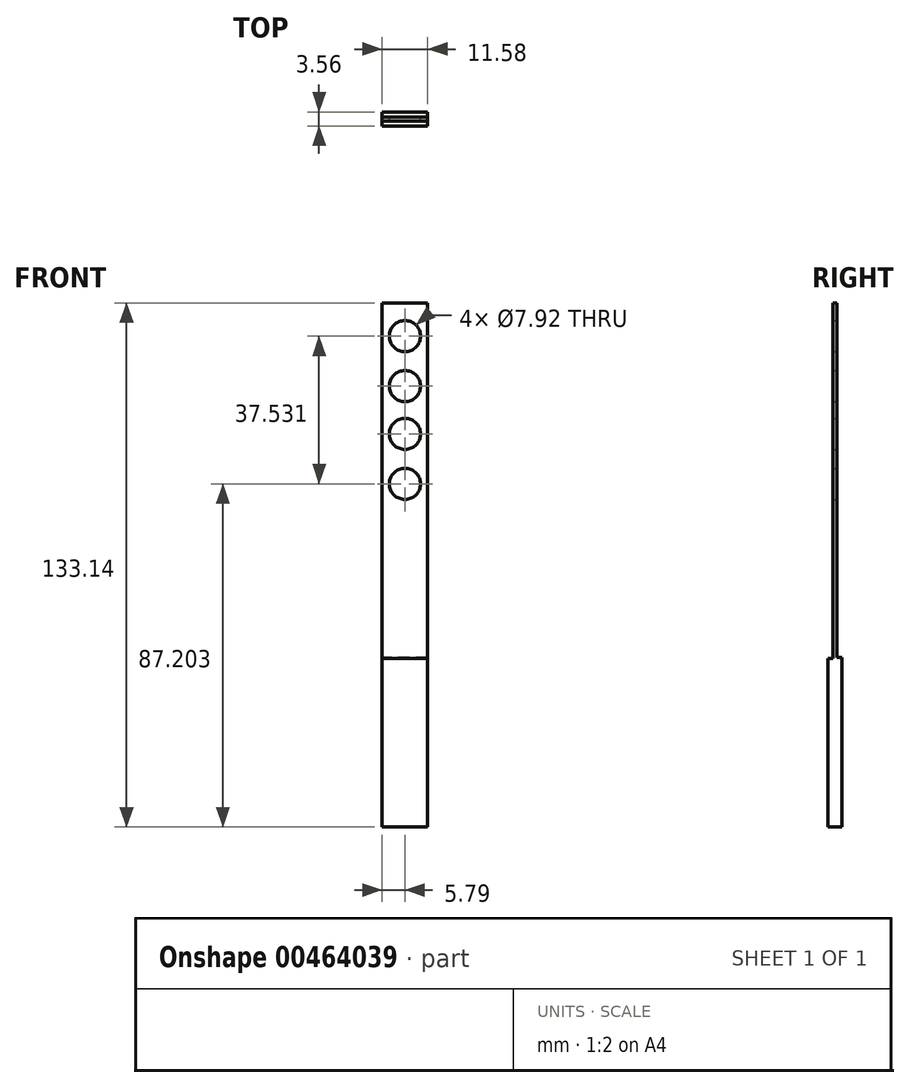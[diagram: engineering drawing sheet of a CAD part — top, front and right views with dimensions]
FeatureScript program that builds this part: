
annotation { "Feature Type Name" : "Feature", "Feature Type Description" : "" }
export const myFeature = defineFeature(function(context is Context, id is Id, definition is map)
    precondition{}
    {
        {
            var Q0;
            Q0=qCreatedBy(makeId("Front.planeOp"),FACE);
            var sketch = newSketch(context, id + "F0", { "sketchPlane" : qUnion([Q0])});
            skLineSegment(sketch, "E0.bottom", {"start": v(-5.79, 66.57) * mm, "end": v(5.79, 66.57) * mm});
            skLineSegment(sketch, "E0.top", {"start": v(-5.79, -66.57) * mm, "end": v(5.79, -66.57) * mm});
            skLineSegment(sketch, "E0.left", {"start": v(-5.79, 66.57) * mm, "end": v(-5.79, -66.57) * mm});
            skLineSegment(sketch, "E0.right", {"start": v(5.79, 66.57) * mm, "end": v(5.79, -66.57) * mm});
            skPoint(sketch, "E0.middle", {"position": v(0, 0) * mm});
            skCircle(sketch, "E1", {"center": v(0, 58.16) * mm, "radius": 3.96 * mm});
            skCircle(sketch, "E2", {"center": v(0, 45.47) * mm, "radius": 3.96 * mm});
            skCircle(sketch, "E3", {"center": v(0, 33.33) * mm, "radius": 3.96 * mm});
            skCircle(sketch, "E4", {"center": v(0, 20.63) * mm, "radius": 3.96 * mm});
            skSolve(sketch);
        }
        {
            var Q0;
            Q0=makeQuery(id+"F0.imprint","IMPRINT",FACE,{"disambiguationData":[TD([[makeQuery(id+"F0.imprint","IMPRINT",EDGE,{"derivedFrom":sQuery(id+"F0.wireOp",EDGE,"E0.bottom")}),-1.0]])]});
            extrude(context, id + "F1", {"entities" : qUnion([Q0]), "depth" : 1.02 * mm});
        }
        {
            var Q0;
            Q0=makeQuery(id+"F1.opExtrude","CAP_FACE",FACE,{"disambiguationData":[OSD([sQuery(id+"F0.wireOp",EDGE,"E0.bottom"),sQuery(id+"F0.wireOp",EDGE,"E0.top"),sQuery(id+"F0.wireOp",EDGE,"E0.left"),sQuery(id+"F0.wireOp",EDGE,"E0.right"),sQuery(id+"F0.wireOp",EDGE,"E1"),sQuery(id+"F0.wireOp",EDGE,"E2"),sQuery(id+"F0.wireOp",EDGE,"E3"),sQuery(id+"F0.wireOp",EDGE,"E4")])],"isStart":false});
            var sketch = newSketch(context, id + "F2", { "sketchPlane" : qUnion([Q0])});
            skLineSegment(sketch, "E5", {"start": v(-5.79, -23.68) * mm, "end": v(5.79, -23.68) * mm});
            skSolve(sketch);
        }
        {
            var Q0;
            Q0 = qSketchRegion(id + "F2", true);
            var Q1;
            {var subQ0=sQuery(id+"F2.wireOp",EDGE,"E5");Q1=makeQuery(id+"F2.imprint","IMPRINT",FACE,{"disambiguationData":[TD([[makeQuery(id+"F2.imprint","IMPRINT",EDGE,{"derivedFrom":subQ0}),-1.0]])]});}
            extrude(context, id + "F3", {"entities" : qUnion([Q0, Q1]), "operationType" : NewBodyOperationType.ADD, "depth" : 1.27 * mm});
        }
        {
            var Q0;
            Q0=makeQuery(id+"F1.opExtrude","CAP_FACE",FACE,{"disambiguationData":[OSD([sQuery(id+"F0.wireOp",EDGE,"E0.bottom"),sQuery(id+"F0.wireOp",EDGE,"E0.top"),sQuery(id+"F0.wireOp",EDGE,"E0.left"),sQuery(id+"F0.wireOp",EDGE,"E0.right"),sQuery(id+"F0.wireOp",EDGE,"E1"),sQuery(id+"F0.wireOp",EDGE,"E2"),sQuery(id+"F0.wireOp",EDGE,"E3"),sQuery(id+"F0.wireOp",EDGE,"E4")])],"isStart":true});
            var sketch = newSketch(context, id + "F4", { "sketchPlane" : qUnion([Q0])});
            skLineSegment(sketch, "E6", {"start": v(-5.79, -23.52) * mm, "end": v(5.79, -23.52) * mm});
            skSolve(sketch);
        }
        {
            var Q0;
            Q0 = qSketchRegion(id + "F4", true);
            var Q1;
            {var subQ0=sQuery(id+"F4.wireOp",EDGE,"E6");Q1=makeQuery(id+"F4.imprint","IMPRINT",FACE,{"disambiguationData":[TD([[makeQuery(id+"F4.imprint","IMPRINT",EDGE,{"derivedFrom":subQ0}),-1.0]])]});}
            extrude(context, id + "F5", {"entities" : qUnion([Q0, Q1]), "operationType" : NewBodyOperationType.ADD, "depth" : 1.27 * mm});
        }
    });
